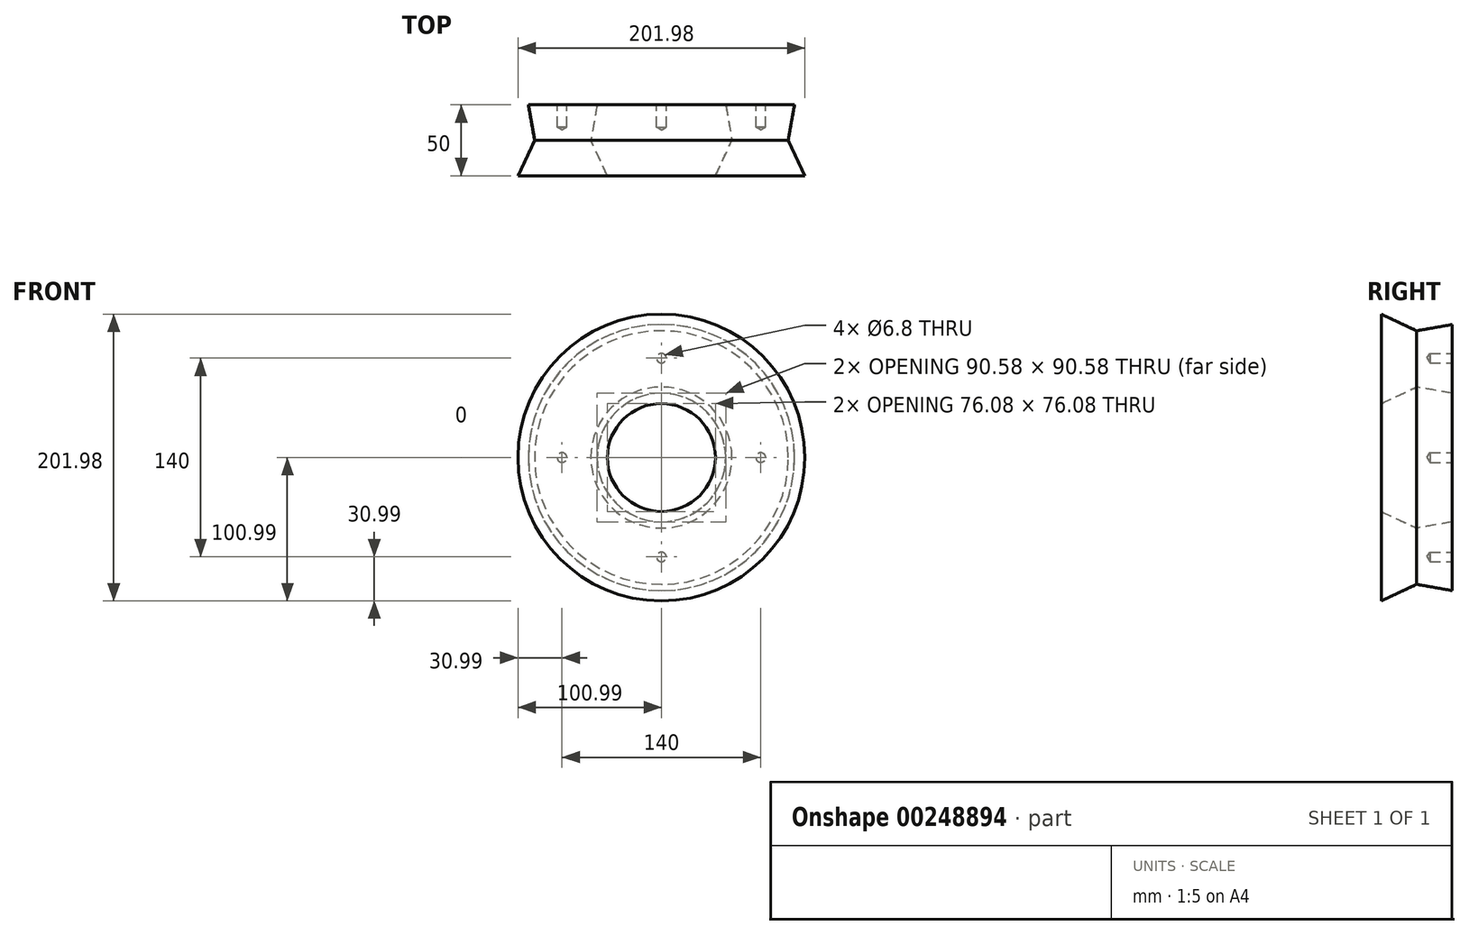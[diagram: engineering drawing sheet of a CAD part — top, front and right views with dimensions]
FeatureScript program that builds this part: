
annotation { "Feature Type Name" : "Feature", "Feature Type Description" : "" }
export const myFeature = defineFeature(function(context is Context, id is Id, definition is map)
    precondition{}
    {
        {
            var Q0;
            Q0=qCreatedBy(makeId("Front.planeOp"),FACE);
            var sketch = newSketch(context, id + "F0", { "sketchPlane" : qUnion([Q0])});
            skCircle(sketch, "E0", {"center": v(0, 0) * mm, "radius": 49.7 * mm});
            skCircle(sketch, "E1", {"center": v(0, 0) * mm, "radius": 89.34 * mm});
            skSolve(sketch);
        }
        {
            var Q0;
            Q0 = qSketchRegion(id + "F0", true);
            extrude(context, id + "F1", {"entities" : qUnion([Q0]), "oppositeDirection" : true, "depth" : 25 * mm, "hasDraft" : true, "draftAngle" : 10 * degree, "hasSecondDirection" : true, "secondDirectionOppositeDirection" : false, "secondDirectionDepth" : 25 * mm, "hasSecondDirectionDraft" : true, "secondDirectionDraftAngle" : 25 * degree});
        }
        {
            var Q0;
            Q0=makeQuery(id+"F1.opExtrude","CAP_FACE",FACE,{"disambiguationData":[OSD([sQuery(id+"F0.wireOp",EDGE,"E0"),sQuery(id+"F0.wireOp",EDGE,"E1")])],"isStart":false});
            var sketch = newSketch(context, id + "F2", { "sketchPlane" : qUnion([Q0])});
            skPoint(sketch, "E2", {"position": v(70, 0) * mm});
            skPoint(sketch, "E3.end.orphan", {"position": v(0, 0) * mm});
            skLineSegment(sketch, "E4", {"start": v(0, 0) * mm, "end": v(70, 0) * mm, "construction": true});
            skSolve(sketch);
        }
        {
            var Q0;
            Q0=sQuery(id+"F2.wireOp",VERTEX,"E2");
            var Q1;
            Q1=makeQuery(id+"F1.*.split.splitOp","SPLIT",BODY,{"derivedFrom":makeQuery(id+"F1.opExtrude","SWEPT_BODY",BODY,{"disambiguationData":[OSD([sQuery(id+"F0.wireOp",EDGE,"E0"),sQuery(id+"F0.wireOp",EDGE,"E1")])]})});
            hole(context, id + "F3", {"style" : HoleStyle.SIMPLE, "endStyle" : HoleEndStyle.BLIND, "standardTappedOrClearance" : lookupTablePath({ "standard" : "ISO", "fit" : "Normal", "engagement" : "75%", "pitch" : "1.25 mm", "size" : "M8", "type" : "Tapped" }), "standardBlindInLast" : lookupTablePath({ "fit" : "Standard", "standard" : "ISO", "engagement" : "75%", "pitch" : "1.25 mm", "size" : "M8", "type" : "Tapped" }), "holeDiameter" : 6.8 * mm, "showTappedDepth" : true, "holeDepth" : 15.75 * mm, "tappedDepth" : 12 * mm, "tapClearance" : 3, "startFromSketch" : true, "locations" : qUnion([Q0]), "scope" : qUnion([Q1]), "majorDiameter" : 8 * mm});
        }
        {
            var Q0;
            Q0=makeQuery(id+"F1.*.split.splitOp","SPLIT",BODY,{"derivedFrom":makeQuery(id+"F1.opExtrude","SWEPT_BODY",BODY,{"disambiguationData":[OSD([sQuery(id+"F0.wireOp",EDGE,"E0"),sQuery(id+"F0.wireOp",EDGE,"E1")])]})});
            var Q1;
            {var subQ0=makeQuery(id+"F1.opExtrude","SWEPT_FACE",FACE,{"disambiguationData":[OSD([sQuery(id+"F0.wireOp",EDGE,"E1")])]});Q1=makeQuery(id+"F1.*.booleanUnion.opBoolean","MERGE",EDGE,{"derivedFrom":[makeQuery(id+"F1.*.split.splitOp","SPLIT_SURFACE_INTERSECT",EDGE,{"derivedFrom":[subQ0]}),makeQuery(id+"F1.*.split.splitOp","SPLIT_SURFACE_INTERSECT",EDGE,{"derivedFrom":[subQ0],"isFromBackBody":true})]});}
            circularPattern(context, id + "F4", {"entities" : qUnion([Q0]), "axis" : qUnion([Q1]), "angle" : 360 * degree, "instanceCount" : 4, "equalSpace" : true});
        }
    });
